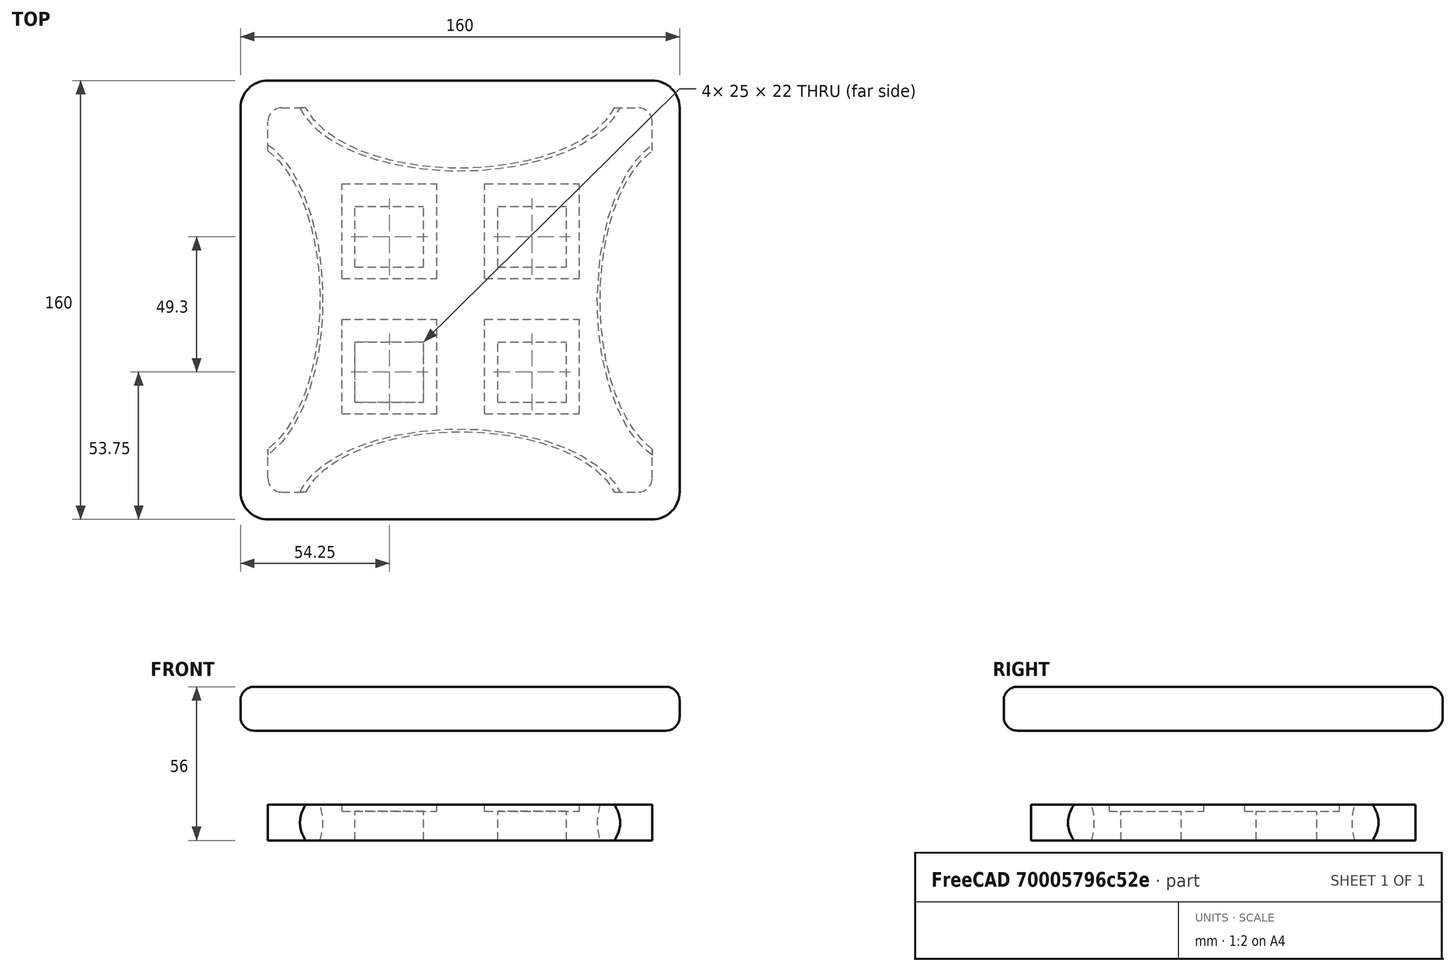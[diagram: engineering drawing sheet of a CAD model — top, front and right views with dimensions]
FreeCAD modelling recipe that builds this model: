
FCSTD DOCUMENT  (FreeCAD 0.17R13541 (Git))
Label: LifelineBody_Bottom
License: All rights reserved
LicenseURL: http://en.wikipedia.org/wiki/All_rights_reserved
objects: Part::Cut×12, Part::Box×10, Part::Ellipsoid×4, Part::Fillet×4
note: 30 computed .brp shape members not serialized (recipe doc carries the construction recipe); baked Part::Feature solids carry a one-line shape summary decoded from their .brp

FEATURE [Part::Box] Box001  label="Base"
  AttacherType = Attacher::AttachEngine3D
  Height = 13
  Length = 140
  Width = 140
FEATURE [Part::Box] Box  label="Cut1"
  AttacherType = Attacher::AttachEngine3D
  Height = 2.4
  Length = 34.5
  Placement = pos=(79,28.5,10.6) rot=(0,0,1;0rad)
  Width = 34.5
FEATURE [Part::Box] Box002  label="Cut2"
  AttacherType = Attacher::AttachEngine3D
  Height = 2.4
  Length = 34.5
  Placement = pos=(79,77.8,10.6) rot=(0,0,1;0rad)
  Width = 34.5
FEATURE [Part::Box] Box003  label="Cut3"
  AttacherType = Attacher::AttachEngine3D
  Height = 2.4
  Length = 34.5
  Placement = pos=(27,28.5,10.6) rot=(0,0,1;0rad)
  Width = 34.5
FEATURE [Part::Box] Box004  label="Cut4"
  AttacherType = Attacher::AttachEngine3D
  Height = 2.4
  Length = 34.5
  Placement = pos=(27,77.8,10.6) rot=(0,0,1;0rad)
  Width = 34.5
FEATURE [Part::Ellipsoid] Ellipsoid
  Angle1 = -90
  Angle2 = 90
  Angle3 = 360
  AttacherType = Attacher::AttachEngine3D
  Placement = pos=(70,147,6.5) rot=(0,0,1;0rad)
  Radius1 = 25
  Radius2 = 60
  Radius3 = 30
FEATURE [Part::Ellipsoid] Ellipsoid001
  Angle1 = -90
  Angle2 = 90
  Angle3 = 360
  AttacherType = Attacher::AttachEngine3D
  Placement = pos=(70,-7,6.5) rot=(0,0,1;0rad)
  Radius1 = 25
  Radius2 = 60
  Radius3 = 30
FEATURE [Part::Cut] Cut
  Base = -> Box001
  Tool = -> Ellipsoid
FEATURE [Part::Cut] Cut001
  Base = -> Cut
  Tool = -> Ellipsoid001
FEATURE [Part::Ellipsoid] Ellipsoid002
  Angle1 = -90
  Angle2 = 90
  Angle3 = 360
  AttacherType = Attacher::AttachEngine3D
  Placement = pos=(-10,70,6.5) rot=(0,0,1;1.5708rad)
  Radius1 = 25
  Radius2 = 60
  Radius3 = 30
FEATURE [Part::Ellipsoid] Ellipsoid003
  Angle1 = -90
  Angle2 = 90
  Angle3 = 360
  AttacherType = Attacher::AttachEngine3D
  Placement = pos=(150,70,6.5) rot=(0,0,1;1.5708rad)
  Radius1 = 25
  Radius2 = 60
  Radius3 = 30
FEATURE [Part::Cut] Cut002
  Base = -> Cut001
  Tool = -> Ellipsoid002
FEATURE [Part::Cut] Cut003
  Base = -> Cut002
  Tool = -> Ellipsoid003
FEATURE [Part::Box] Box005  label="Cut004"
  AttacherType = Attacher::AttachEngine3D
  Height = 13
  Length = 25
  Placement = pos=(83.75,82.05,0) rot=(0,0,1;0rad)
  Width = 22
FEATURE [Part::Box] Box006  label="Cut005"
  AttacherType = Attacher::AttachEngine3D
  Height = 13
  Length = 25
  Placement = pos=(83.75,32.75,0) rot=(0,0,1;0rad)
  Width = 22
FEATURE [Part::Box] Box007  label="Cut006"
  AttacherType = Attacher::AttachEngine3D
  Height = 13
  Length = 25
  Placement = pos=(31.75,32.75,0) rot=(0,0,1;0rad)
  Width = 22
FEATURE [Part::Box] Box008  label="Cut007"
  AttacherType = Attacher::AttachEngine3D
  Height = 13
  Length = 25
  Placement = pos=(31.75,82.05,0) rot=(0,0,1;0rad)
  Width = 22
FEATURE [Part::Box] Box009  label="Base001"
  AttacherType = Attacher::AttachEngine3D
  Height = 16
  Length = 160
  Width = 160
FEATURE [Part::Fillet] Fillet
  Base = -> Box009
  Edges = 4 edges r=10: [Edge1,Edge3,Edge5,Edge7]
FEATURE [Part::Fillet] Fillet001
  Base = -> Fillet
  Edges = 8 edges r=5: [Edge1,Edge5,Edge6,Edge7,Edge8,Edge9,Edge10,Edge11]
FEATURE [Part::Fillet] Fillet002  label="Top"
  Base = -> Fillet001
  Edges = 8 edges r=5: [Edge3,Edge6,Edge11,Edge12,Edge13,Edge14,Edge15,Edge16]
  Placement = pos=(-10,-10,40) rot=(0,0,1;0rad)
FEATURE [Part::Fillet] Fillet003
  Base = -> Cut003
  Edges = 4 edges r=5: [Edge4,Edge30,Edge32,Edge35]
FEATURE [Part::Cut] Cut004  label="Cut008"
  Base = -> Fillet003
  Tool = -> Box003
FEATURE [Part::Cut] Cut005  label="Cut009"
  Base = -> Cut004
  Tool = -> Box004
FEATURE [Part::Cut] Cut006  label="Cut010"
  Base = -> Cut005
  Tool = -> Box
FEATURE [Part::Cut] Cut007  label="Cut011"
  Base = -> Cut006
  Tool = -> Box002
FEATURE [Part::Cut] Cut008  label="Cut012"
  Base = -> Cut007
  Tool = -> Box008
FEATURE [Part::Cut] Cut009  label="Cut013"
  Base = -> Cut008
  Tool = -> Box007
FEATURE [Part::Cut] Cut010  label="Cut014"
  Base = -> Cut009
  Tool = -> Box005
FEATURE [Part::Cut] Cut011  label="Cut015"
  Base = -> Cut010
  Tool = -> Box006
